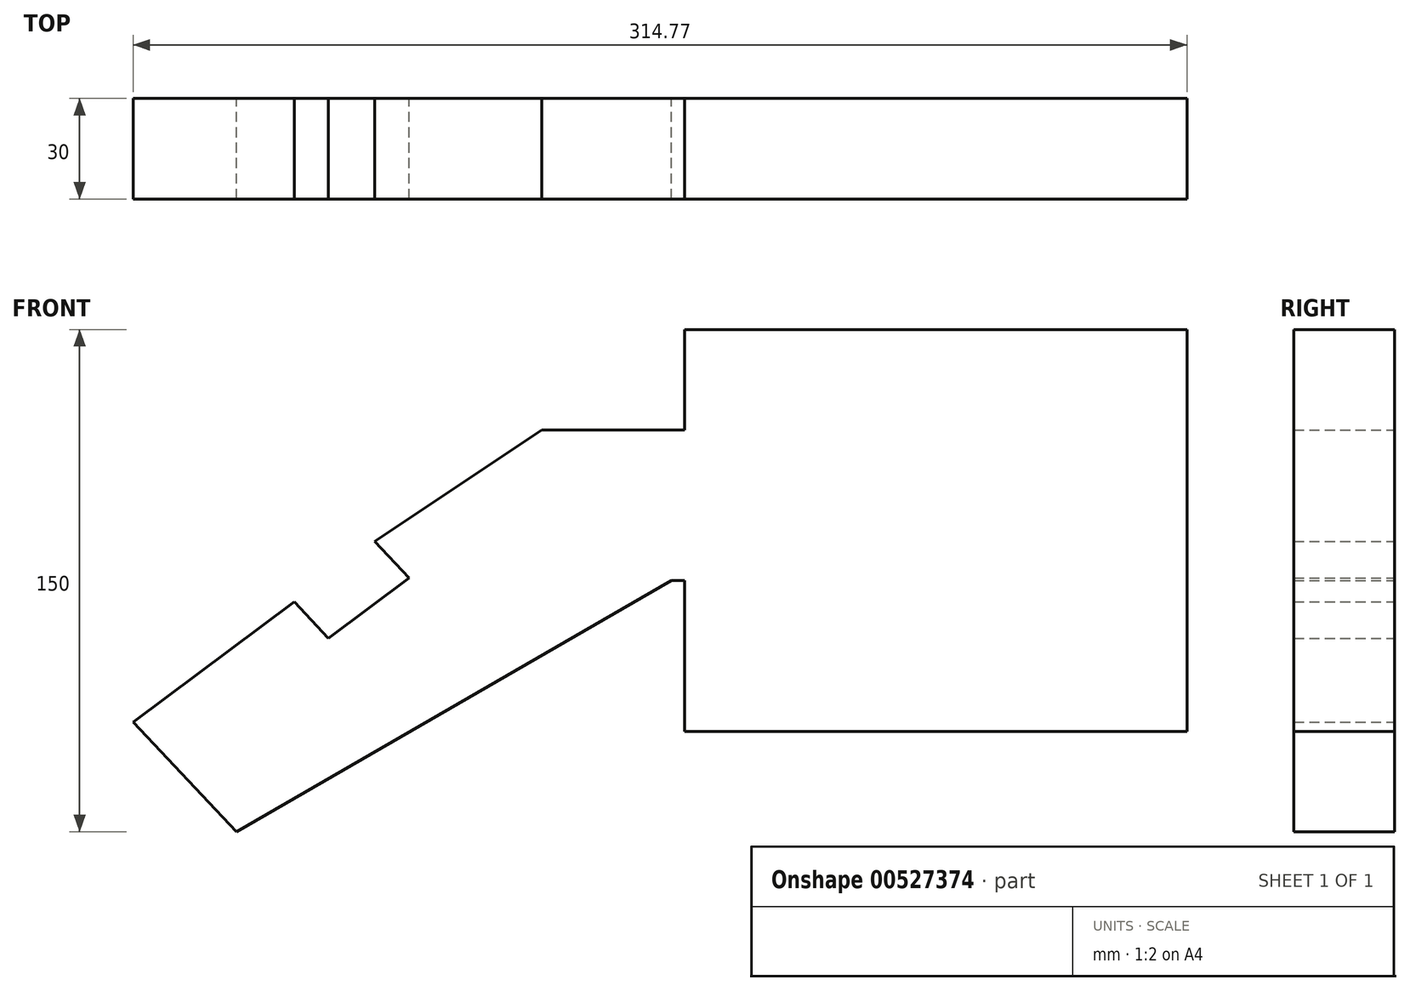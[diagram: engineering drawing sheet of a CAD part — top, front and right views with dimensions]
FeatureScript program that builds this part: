
annotation { "Feature Type Name" : "Feature", "Feature Type Description" : "" }
export const myFeature = defineFeature(function(context is Context, id is Id, definition is map)
    precondition{}
    {
        {
            var Q0;
            Q0=qCreatedBy(makeId("Front.planeOp"),FACE);
            var sketch = newSketch(context, id + "F0", { "sketchPlane" : qUnion([Q0])});
            skLineSegment(sketch, "E0", {"start": v(-164.77, -32.72) * mm, "end": v(-133.95, -65.5) * mm});
            skLineSegment(sketch, "E1", {"start": v(-164.77, -32.72) * mm, "end": v(-116.7, 3.2) * mm});
            skLineSegment(sketch, "E2", {"start": v(-116.7, 3.2) * mm, "end": v(-106.43, -7.74) * mm});
            skLineSegment(sketch, "E3", {"start": v(-106.43, -7.74) * mm, "end": v(-82.4, 10.22) * mm});
            skLineSegment(sketch, "E4", {"start": v(-82.4, 10.22) * mm, "end": v(-92.67, 21.15) * mm});
            skLineSegment(sketch, "E5", {"start": v(-92.67, 21.15) * mm, "end": v(-42.78, 54.5) * mm});
            skLineSegment(sketch, "E6", {"start": v(-133.95, -65.5) * mm, "end": v(-4.05, 9.5) * mm});
            skLineSegment(sketch, "E7", {"start": v(-42.78, 54.5) * mm, "end": v(77.22, 54.5) * mm});
            skLineSegment(sketch, "E8", {"start": v(77.22, 54.5) * mm, "end": v(77.22, 9.5) * mm});
            skLineSegment(sketch, "E9", {"start": v(0, 9.5) * mm, "end": v(-4.05, 9.5) * mm});
            skLineSegment(sketch, "E10", {"start": v(0, 54.5) * mm, "end": v(0, 84.5) * mm});
            skLineSegment(sketch, "E11", {"start": v(0, 84.5) * mm, "end": v(150, 84.5) * mm});
            skLineSegment(sketch, "E12", {"start": v(150, 84.5) * mm, "end": v(150, -35.5) * mm});
            skLineSegment(sketch, "E13", {"start": v(150, -35.5) * mm, "end": v(0, -35.5) * mm});
            skLineSegment(sketch, "E14", {"start": v(0, -35.5) * mm, "end": v(0, 9.5) * mm});
            skLineSegment(sketch, "E15", {"start": v(-4.05, 9.5) * mm, "end": v(77.22, 9.5) * mm});
            skSolve(sketch);
        }
        {
            var Q0;
            {var subQ2=sQuery(id+"F0.wireOp",EDGE,"E8");Q0=makeQuery(id+"F0.imprint","IMPRINT",FACE,{"disambiguationData":[TD([[makeQuery(id+"F0.imprint","IMPRINT",EDGE,{"derivedFrom":subQ2}),1.0]])]});}
            extrude(context, id + "F1", {"entities" : qUnion([Q0]), "depth" : 30 * mm, "offsetDistance" : 25 * mm});
        }
        {
            var Q0;
            Q0 = qSketchRegion(id + "F0", true);
            extrude(context, id + "F2", {"entities" : qUnion([Q0]), "operationType" : NewBodyOperationType.ADD, "depth" : 30 * mm, "offsetDistance" : 25 * mm});
        }
    });
